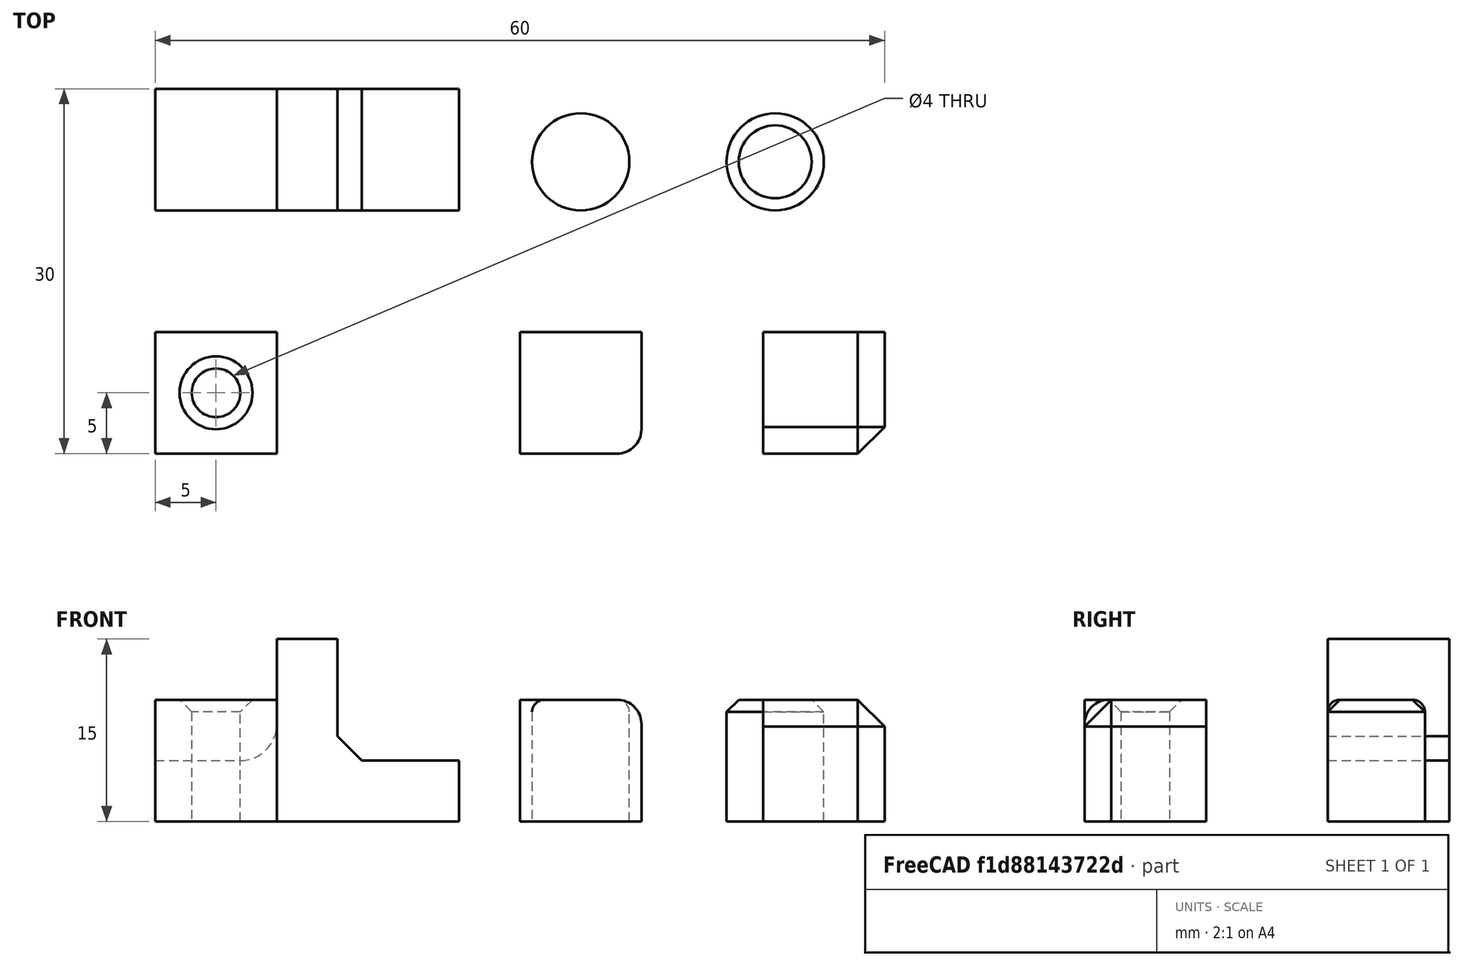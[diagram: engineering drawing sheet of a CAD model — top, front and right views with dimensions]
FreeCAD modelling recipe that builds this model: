
FCSTD DOCUMENT  (FreeCAD 0.21R33694 (Git))
Label: OJT1_T12P01_figures
License: All rights reserved
LicenseURL: http://en.wikipedia.org/wiki/All_rights_reserved
objects: Part::Box×6, Part::Chamfer×5, Part::Cylinder×3, Part::Cut×3, Part::Fillet×3
note: 20 computed .brp shape members not serialized (recipe doc carries the construction recipe); baked Part::Feature solids carry a one-line shape summary decoded from their .brp

FEATURE [Part::Box] Box  label="Cube"
  AttacherType = Attacher::AttachEngine3D
  Height = 10
  Length = 10
  Width = 10
FEATURE [Part::Cylinder] Cylinder
  Angle = 360
  AttacherType = Attacher::AttachEngine3D
  FirstAngle = 0
  Height = 10
  Placement = pos=(5,5,0) rot=(0,0,1;0rad)
  Radius = 2
  SecondAngle = 0
FEATURE [Part::Cut] Cut
  Base = -> Box
  Refine = true
  Tool = -> Cylinder
FEATURE [Part::Box] Box001  label="Cube001"
  AttacherType = Attacher::AttachEngine3D
  Height = 10
  Length = 10
  Placement = pos=(30,0,0) rot=(0,0,1;0rad)
  Width = 10
FEATURE [Part::Box] Box002  label="Cube002"
  AttacherType = Attacher::AttachEngine3D
  Height = 15
  Length = 25
  Placement = pos=(0,20,0) rot=(0,0,1;0rad)
  Width = 10
FEATURE [Part::Box] Box003  label="Cube003"
  AttacherType = Attacher::AttachEngine3D
  Height = 10
  Length = 10
  Placement = pos=(15,20,5) rot=(0,0,1;0rad)
  Width = 10
FEATURE [Part::Box] Box004  label="Cube004"
  AttacherType = Attacher::AttachEngine3D
  Height = 10
  Length = 10
  Placement = pos=(0,20,5) rot=(0,0,1;0rad)
  Width = 10
FEATURE [Part::Cut] Cut001
  Base = -> Box002
  Refine = true
  Tool = -> Box003
FEATURE [Part::Cut] Cut002
  Base = -> Cut001
  Refine = true
  Tool = -> Box004
FEATURE [Part::Cylinder] Cylinder001
  Angle = 360
  AttacherType = Attacher::AttachEngine3D
  FirstAngle = 0
  Height = 10
  Placement = pos=(35,24,0) rot=(0,0,1;0rad)
  Radius = 4
  SecondAngle = 0
FEATURE [Part::Cylinder] Cylinder002
  Angle = 360
  AttacherType = Attacher::AttachEngine3D
  FirstAngle = 0
  Height = 10
  Placement = pos=(51,24,0) rot=(0,0,1;0rad)
  Radius = 4
  SecondAngle = 0
FEATURE [Part::Chamfer] Chamfer
  Base = -> Cut
  Edges = 1 edges r=1: [Edge10]
FEATURE [Part::Chamfer] Chamfer001
  Base = -> Box001
  Edges = 3 edges r=2: [Edge5,Edge6,Edge10]
FEATURE [Part::Fillet] Fillet
  Base = -> Box001
  Edges = 3 edges r=2: [Edge5,Edge6,Edge10]
FEATURE [Part::Box] Box005  label="Cube005"
  AttacherType = Attacher::AttachEngine3D
  Height = 10
  Length = 10
  Placement = pos=(50,0,0) rot=(0,0,1;0rad)
  Width = 10
FEATURE [Part::Chamfer] Chamfer002
  Base = -> Box005
  Edges = 3 edges r=2.2: [Edge5,Edge6,Edge10]
FEATURE [Part::Chamfer] Chamfer003
  Base = -> Cylinder002
  Edges = 1 edges r=1: [Edge3]
FEATURE [Part::Fillet] Fillet001
  Base = -> Cylinder001
  Edges = 1 edges r=1: [Edge3]
FEATURE [Part::Chamfer] Chamfer004
  Base = -> Cut002
  Edges = 1 edges r=2: [Edge22]
FEATURE [Part::Fillet] Fillet002
  Base = -> Chamfer004
  Edges = 1 edges r=3: [Edge26]
